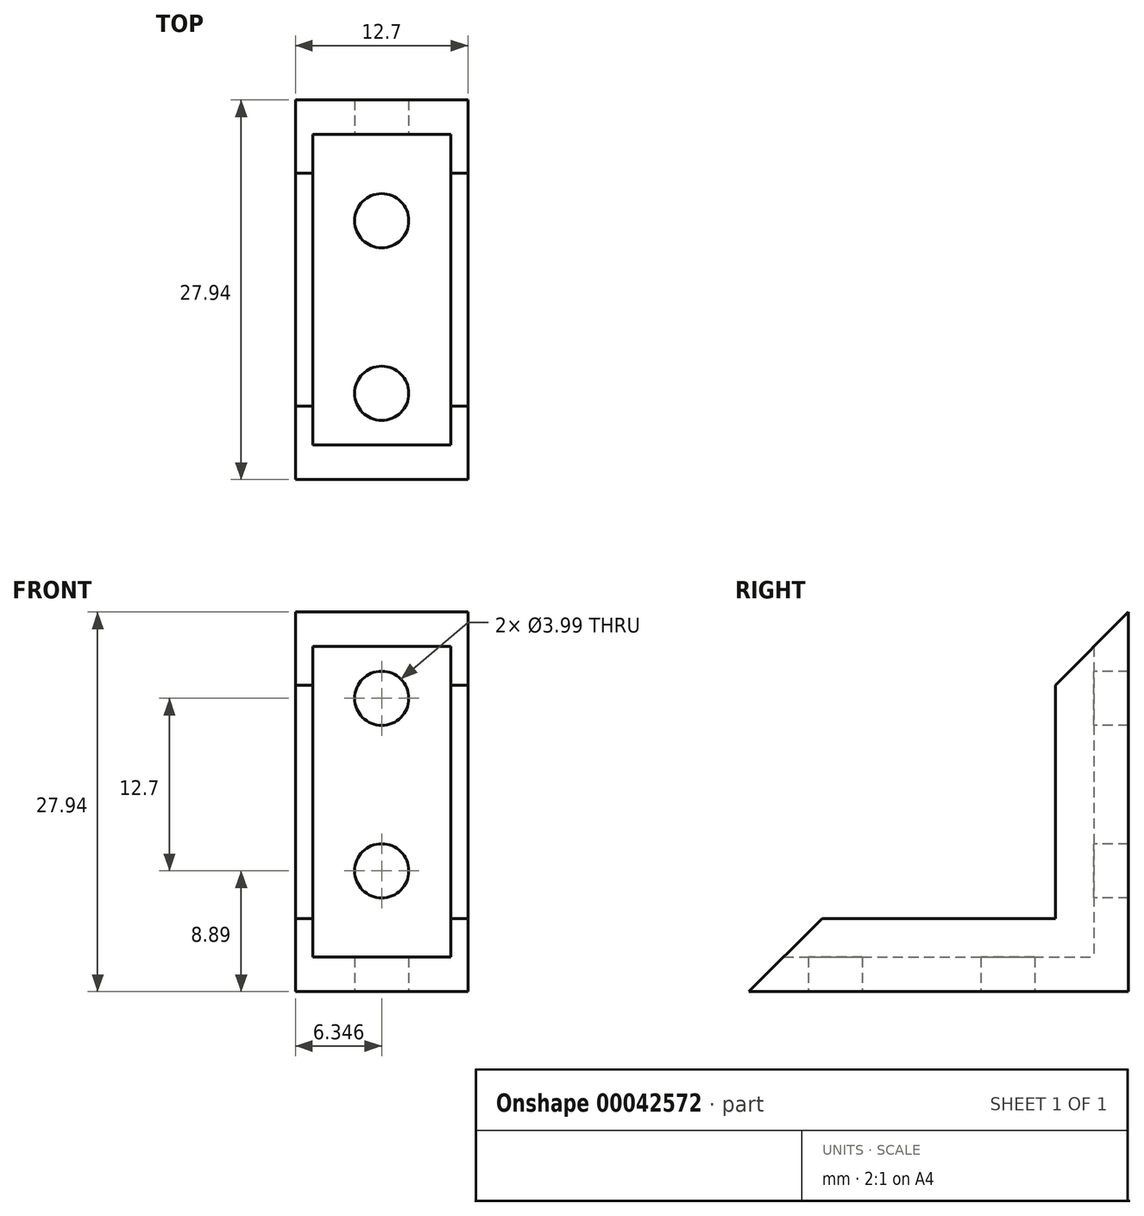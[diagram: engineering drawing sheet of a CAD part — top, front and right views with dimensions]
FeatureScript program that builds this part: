
annotation { "Feature Type Name" : "Feature", "Feature Type Description" : "" }
export const myFeature = defineFeature(function(context is Context, id is Id, definition is map)
    precondition{}
    {
        {
            var Q0;
            Q0=qCreatedBy(makeId("Top.planeOp"),FACE);
            var sketch = newSketch(context, id + "F0", { "sketchPlane" : qUnion([Q0])});
            skLineSegment(sketch, "E0.bottom", {"start": v(-383.42, 154.2) * mm, "end": v(-370.72, 154.2) * mm});
            skLineSegment(sketch, "E0.top", {"start": v(-383.42, 182.13) * mm, "end": v(-370.72, 182.13) * mm});
            skLineSegment(sketch, "E0.left", {"start": v(-383.42, 154.2) * mm, "end": v(-383.42, 182.13) * mm});
            skLineSegment(sketch, "E0.right", {"start": v(-370.72, 154.2) * mm, "end": v(-370.72, 182.13) * mm});
            skLineSegment(sketch, "E1", {"start": v(-383.42, 163.22) * mm, "end": v(-382.15, 163.22) * mm});
            skLineSegment(sketch, "E2", {"start": v(-377.07, 182.13) * mm, "end": v(-377.07, 179.6) * mm});
            skLineSegment(sketch, "E3", {"start": v(-382.15, 154.2) * mm, "end": v(-382.15, 179.6) * mm});
            skLineSegment(sketch, "E4", {"start": v(-382.15, 179.6) * mm, "end": v(-377.07, 179.6) * mm});
            skLineSegment(sketch, "E5.MirrorCS", {"start": v(-372, 179.6) * mm, "end": v(-377.07, 179.6) * mm});
            skLineSegment(sketch, "E6.MirrorCS", {"start": v(-372, 154.2) * mm, "end": v(-372, 179.6) * mm});
            skLineSegment(sketch, "E7", {"start": v(-377.07, 179.6) * mm, "end": v(-377.07, 173.24) * mm});
            skLineSegment(sketch, "E8", {"start": v(-377.07, 154.2) * mm, "end": v(-377.07, 160.54) * mm});
            skLineSegment(sketch, "E9", {"start": v(-377.07, 173.24) * mm, "end": v(-377.07, 160.54) * mm});
            skCircle(sketch, "E10", {"center": v(-377.07, 173.24) * mm, "radius": 2 * mm});
            skCircle(sketch, "E11", {"center": v(-377.07, 160.54) * mm, "radius": 2 * mm});
            skSolve(sketch);
        }
        {
            var Q0;
            {var subQ14=sQuery(id+"F0.wireOp",EDGE,"E4");Q0=makeQuery(id+"F0.imprint","IMPRINT",FACE,{"disambiguationData":[TD([[makeQuery(id+"F0.imprint","IMPRINT",EDGE,{"derivedFrom":subQ14}),-1.0]])]});}
            var Q1;
            {var subQ11=sQuery(id+"F0.wireOp",EDGE,"E5.MirrorCS");Q1=makeQuery(id+"F0.imprint","IMPRINT",FACE,{"disambiguationData":[TD([[makeQuery(id+"F0.imprint","IMPRINT",EDGE,{"derivedFrom":subQ11}),1.0]])]});}
            extrude(context, id + "F1", {"entities" : qUnion([Q0, Q1]), "depth" : 2.54 * mm});
        }
        {
            var Q0;
            {var subQ2=sQuery(id+"F0.wireOp",EDGE,"E1");Q0=makeQuery(id+"F0.imprint","IMPRINT",FACE,{"disambiguationData":[TD([[makeQuery(id+"F0.imprint","IMPRINT",EDGE,{"derivedFrom":subQ2}),1.0]])]});}
            var Q1;
            {var subQ3=sQuery(id+"F0.wireOp",EDGE,"E0.right");Q1=makeQuery(id+"F0.imprint","IMPRINT",FACE,{"disambiguationData":[TD([[makeQuery(id+"F0.imprint","IMPRINT",EDGE,{"derivedFrom":subQ3}),1.0]])]});}
            var Q2;
            {var subQ3=sQuery(id+"F0.wireOp",EDGE,"E1");Q2=makeQuery(id+"F0.imprint","IMPRINT",FACE,{"disambiguationData":[TD([[makeQuery(id+"F0.imprint","IMPRINT",EDGE,{"derivedFrom":subQ3}),-1.0]])]});}
            extrude(context, id + "F2", {"entities" : qUnion([Q0, Q1, Q2]), "operationType" : NewBodyOperationType.ADD, "depth" : 27.94 * mm});
        }
        {
            var Q0;
            Q0=makeQuery(id+"F2.opExtrude","SWEPT_FACE",FACE,{"disambiguationData":[OSD([sQuery(id+"F0.wireOp",EDGE,"E4"),sQuery(id+"F0.wireOp",EDGE,"E5.MirrorCS")])]});
            var sketch = newSketch(context, id + "F3", { "sketchPlane" : qUnion([Q0])});
            skLineSegment(sketch, "E12", {"start": v(-377.07, 2.54) * mm, "end": v(-377.07, 8.9) * mm});
            skLineSegment(sketch, "E13", {"start": v(-377.07, 27.94) * mm, "end": v(-377.07, 21.6) * mm});
            skLineSegment(sketch, "E14", {"start": v(-377.07, 21.6) * mm, "end": v(-377.07, 8.9) * mm});
            skCircle(sketch, "E15", {"center": v(-377.07, 21.6) * mm, "radius": 2 * mm});
            skCircle(sketch, "E16", {"center": v(-377.07, 8.9) * mm, "radius": 2 * mm});
            skSolve(sketch);
        }
        {
            var Q0;
            {var subQ1=sQuery(id+"F3.wireOp",EDGE,"E14");var subQ3=sQuery(id+"F3.wireOp",EDGE,"E13");var subQ5=makeQuery(id+"F3.imprint","INTERSECT",VERTEX,{"derivedFrom":[subQ3,subQ1]});Q0=makeQuery(id+"F3.imprint","IMPRINT",FACE,{"disambiguationData":[TD([[makeQuery(id+"F3.imprint","IMPRINT",EDGE,{"disambiguationData":[TD([[subQ5,1.0]])],"derivedFrom":subQ3}),1.0]])]});}
            var Q1;
            {var subQ0=sQuery(id+"F3.wireOp",EDGE,"E14");var subQ3=sQuery(id+"F3.wireOp",EDGE,"E13");var subQ4=makeQuery(id+"F3.imprint","INTERSECT",VERTEX,{"derivedFrom":[subQ3,subQ0]});Q1=makeQuery(id+"F3.imprint","IMPRINT",FACE,{"disambiguationData":[TD([[makeQuery(id+"F3.imprint","IMPRINT",EDGE,{"disambiguationData":[TD([[subQ4,1.0]])],"derivedFrom":subQ3}),-1.0]])]});}
            var Q2;
            {var subQ1=sQuery(id+"F3.wireOp",EDGE,"E14");var subQ3=sQuery(id+"F3.wireOp",EDGE,"E12");var subQ5=makeQuery(id+"F3.imprint","INTERSECT",VERTEX,{"derivedFrom":[subQ3,subQ1]});Q2=makeQuery(id+"F3.imprint","IMPRINT",FACE,{"disambiguationData":[TD([[makeQuery(id+"F3.imprint","IMPRINT",EDGE,{"disambiguationData":[TD([[subQ5,1.0]])],"derivedFrom":subQ3}),1.0]])]});}
            var Q3;
            {var subQ1=sQuery(id+"F3.wireOp",EDGE,"E14");var subQ3=sQuery(id+"F3.wireOp",EDGE,"E12");var subQ5=makeQuery(id+"F3.imprint","INTERSECT",VERTEX,{"derivedFrom":[subQ3,subQ1]});Q3=makeQuery(id+"F3.imprint","IMPRINT",FACE,{"disambiguationData":[TD([[makeQuery(id+"F3.imprint","IMPRINT",EDGE,{"disambiguationData":[TD([[subQ5,1.0]])],"derivedFrom":subQ3}),-1.0]])]});}
            extrude(context, id + "F4", {"entities" : qUnion([Q0, Q1, Q2, Q3]), "operationType" : NewBodyOperationType.REMOVE, "oppositeDirection" : true, "depth" : 25.4 * mm});
        }
        {
            var Q0;
            Q0=makeQuery(id+"F2.opExtrude","SWEPT_FACE",FACE,{"disambiguationData":[OSD([sQuery(id+"F0.wireOp",EDGE,"E0.left")])]});
            var sketch = newSketch(context, id + "F5", { "sketchPlane" : qUnion([Q0])});
            skLineSegment(sketch, "E17", {"start": v(-154.2, 0) * mm, "end": v(-159.58, 5.39) * mm});
            skLineSegment(sketch, "E18", {"start": v(-182.13, 27.94) * mm, "end": v(-176.75, 22.55) * mm});
            skLineSegment(sketch, "E19", {"start": v(-182.13, 0) * mm, "end": v(-176.75, 5.39) * mm});
            skLineSegment(sketch, "E20", {"start": v(-159.58, 5.39) * mm, "end": v(-176.75, 5.39) * mm});
            skLineSegment(sketch, "E21", {"start": v(-176.75, 5.39) * mm, "end": v(-176.75, 22.55) * mm});
            skSolve(sketch);
        }
        {
            var Q0;
            Q0=makeQuery(id+"F5.imprint","IMPRINT",FACE,{"disambiguationData":[TD([[makeQuery(id+"F5.imprint","IMPRINT",EDGE,{"derivedFrom":sQuery(id+"F5.wireOp",EDGE,"E17")}),-1.0]])]});
            extrude(context, id + "F6", {"entities" : qUnion([Q0]), "operationType" : NewBodyOperationType.REMOVE, "oppositeDirection" : true, "depth" : 38.1 * mm});
        }
    });
